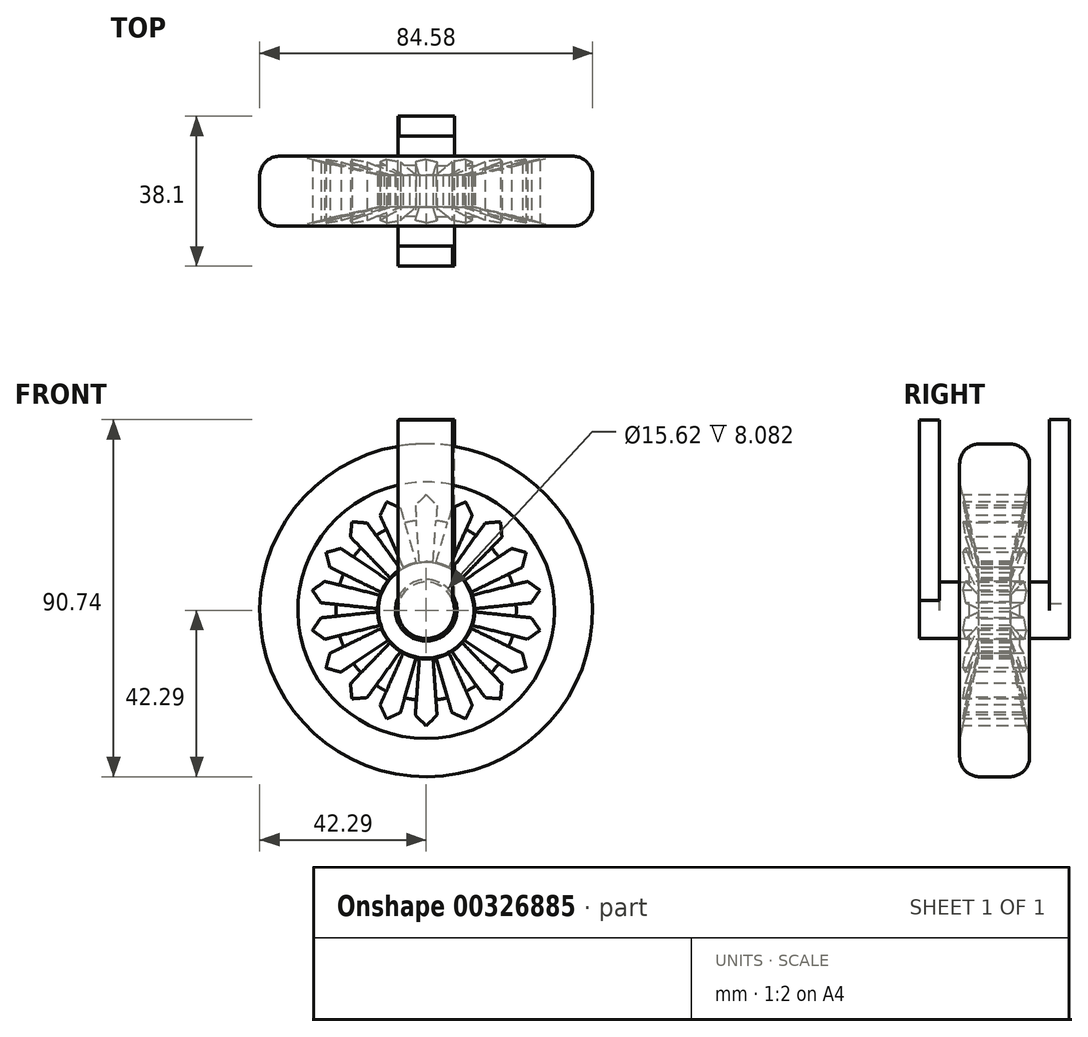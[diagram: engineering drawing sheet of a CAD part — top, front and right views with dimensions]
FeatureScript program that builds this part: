
annotation { "Feature Type Name" : "Feature", "Feature Type Description" : "" }
export const myFeature = defineFeature(function(context is Context, id is Id, definition is map)
    precondition{}
    {
        {
            var Q0;
            Q0=qCreatedBy(makeId("Right.planeOp"),FACE);
            var sketch = newSketch(context, id + "F0", { "sketchPlane" : qUnion([Q0])});
            skPoint(sketch, "E0.middle", {"position": v(0, 21.28) * mm});
            skLineSegment(sketch, "E1.bottom", {"start": v(8.9, 42.3) * mm, "end": v(-8.9, 42.3) * mm});
            skLineSegment(sketch, "E1.left", {"start": v(8.9, 42.3) * mm, "end": v(8.9, 32.6) * mm});
            skLineSegment(sketch, "E1.right", {"start": v(-8.9, 42.3) * mm, "end": v(-8.9, 32.6) * mm});
            skPoint(sketch, "E1.middle", {"position": v(0, 32.6) * mm});
            skLineSegment(sketch, "E2.bottom", {"start": v(4.04, 7.81) * mm, "end": v(-4.04, 7.81) * mm});
            skLineSegment(sketch, "E2.left", {"start": v(4.04, 7.81) * mm, "end": v(4.04, 9.97) * mm});
            skLineSegment(sketch, "E2.right", {"start": v(-4.04, 7.81) * mm, "end": v(-4.04, 9.97) * mm});
            skPoint(sketch, "E2.middle", {"position": v(0, 9.97) * mm});
            skPoint(sketch, "E3.orphan", {"position": v(6.47, 32.6) * mm});
            skPoint(sketch, "E4.orphan", {"position": v(-6.47, 32.6) * mm});
            skPoint(sketch, "E5.orphan", {"position": v(-4.04, 12.12) * mm});
            skPoint(sketch, "E6.orphan", {"position": v(4.04, 12.12) * mm});
            skPoint(sketch, "E7.orphan", {"position": v(-8.9, 22.9) * mm});
            skPoint(sketch, "E1.top.start.orphan", {"position": v(8.9, 22.9) * mm});
            skLineSegment(sketch, "E8", {"start": v(-4.04, 9.97) * mm, "end": v(-4.04, 12.12) * mm});
            skLineSegment(sketch, "E9", {"start": v(4.04, 9.97) * mm, "end": v(4.04, 12.12) * mm});
            skLineSegment(sketch, "E10", {"start": v(4.04, 12.12) * mm, "end": v(6.47, 22.9) * mm});
            skLineSegment(sketch, "E11", {"start": v(8.9, 32.6) * mm, "end": v(6.47, 22.9) * mm});
            skLineSegment(sketch, "E12", {"start": v(-8.9, 32.6) * mm, "end": v(-6.47, 22.9) * mm});
            skLineSegment(sketch, "E13", {"start": v(-6.47, 22.9) * mm, "end": v(-4.04, 12.12) * mm});
            skPoint(sketch, "E0.right.end.orphan", {"position": v(-6.47, 9.97) * mm});
            skPoint(sketch, "E0.left.end.orphan", {"position": v(6.47, 9.97) * mm});
            skLineSegment(sketch, "E14", {"start": v(-3.92, 0) * mm, "end": v(4.17, 0) * mm, "construction": true});
            skSolve(sketch);
        }
        {
            var Q0;
            Q0=makeQuery(id+"F0.imprint","IMPRINT",FACE,{"disambiguationData":[TD([[makeQuery(id+"F0.imprint","IMPRINT",EDGE,{"derivedFrom":sQuery(id+"F0.wireOp",EDGE,"E1.bottom")}),1.0]])]});
            var Q1;
            Q1=sQuery(id+"F0.wireOp",EDGE,"E14");
            revolve(context, id + "F1", {"entities" : qUnion([Q0]), "axis" : qUnion([Q1]), "revolveType" : RevolveType.FULL});
        }
        {
            var Q0;
            Q0=qCreatedBy(makeId("Front.planeOp"),FACE);
            var sketch = newSketch(context, id + "F2", { "sketchPlane" : qUnion([Q0])});
            skLineSegment(sketch, "E15", {"start": v(-1.74, 12.25) * mm, "end": v(-2.76, 26.64) * mm});
            skLineSegment(sketch, "E16", {"start": v(-2.76, 26.64) * mm, "end": v(0, 29.36) * mm});
            skLineSegment(sketch, "E17", {"start": v(-1.74, 12.25) * mm, "end": v(0, 12.38) * mm});
            skLineSegment(sketch, "E18.MirrorCS", {"start": v(2.76, 26.64) * mm, "end": v(0, 29.36) * mm});
            skLineSegment(sketch, "E19.MirrorCS", {"start": v(1.74, 12.25) * mm, "end": v(2.76, 26.64) * mm});
            skLineSegment(sketch, "E20.MirrorCS", {"start": v(1.74, 12.25) * mm, "end": v(0, 12.38) * mm});
            skSolve(sketch);
        }
        {
            var Q0;
            Q0 = qSketchRegion(id + "F2", true);
            extrude(context, id + "F3", {"entities" : qUnion([Q0]), "operationType" : NewBodyOperationType.REMOVE, "endBound" : BoundingType.SYMMETRIC, "oppositeDirection" : true, "depth" : 25.4 * mm});
        }
        {
            var Q0;
            Q0=makeQuery(id+"F3.boolean.opBoolean","COPY",FACE,{"derivedFrom":makeQuery(id+"F3.opExtrude","SWEPT_FACE",FACE,{"disambiguationData":[OSD([sQuery(id+"F2.wireOp",EDGE,"E16")])]})});
            var Q1;
            Q1=makeQuery(id+"F3.boolean.opBoolean","COPY",FACE,{"derivedFrom":makeQuery(id+"F3.opExtrude","SWEPT_FACE",FACE,{"disambiguationData":[OSD([sQuery(id+"F2.wireOp",EDGE,"E18.MirrorCS")])]})});
            var Q2;
            Q2=makeQuery(id+"F3.boolean.opBoolean","COPY",FACE,{"derivedFrom":makeQuery(id+"F3.opExtrude","SWEPT_FACE",FACE,{"disambiguationData":[OSD([sQuery(id+"F2.wireOp",EDGE,"E15")])]})});
            var Q3;
            Q3=makeQuery(id+"F3.boolean.opBoolean","COPY",FACE,{"derivedFrom":makeQuery(id+"F3.opExtrude","SWEPT_FACE",FACE,{"disambiguationData":[OSD([sQuery(id+"F2.wireOp",EDGE,"E17")])]})});
            var Q4;
            Q4=makeQuery(id+"F3.boolean.opBoolean","COPY",FACE,{"derivedFrom":makeQuery(id+"F3.opExtrude","SWEPT_FACE",FACE,{"disambiguationData":[OSD([sQuery(id+"F2.wireOp",EDGE,"E20.MirrorCS")])]})});
            var Q5;
            Q5=makeQuery(id+"F3.boolean.opBoolean","COPY",FACE,{"derivedFrom":makeQuery(id+"F3.opExtrude","SWEPT_FACE",FACE,{"disambiguationData":[OSD([sQuery(id+"F2.wireOp",EDGE,"E19.MirrorCS")])]})});
            var Q6;
            Q6=makeQuery(id+"F1.opRevolve","SWEPT_FACE",FACE,{"disambiguationData":[OSD([sQuery(id+"F0.wireOp",EDGE,"E13")])]});
            circularPattern(context, id + "F4", {"patternType" : PatternType.FACE, "faces" : qUnion([Q0, Q1, Q2, Q3, Q4, Q5]), "axis" : qUnion([Q6]), "angle" : 360 * degree, "instanceCount" : 18, "equalSpace" : true});
        }
        {
            var Q0;
            Q0=makeQuery(id+"F1.opRevolve","SWEPT_FACE",FACE,{"disambiguationData":[OSD([sQuery(id+"F0.wireOp",EDGE,"E1.bottom")])]});
            var Q1;
            Q1=makeQuery(id+"F1.opRevolve","SWEPT_FACE",FACE,{"disambiguationData":[OSD([sQuery(id+"F0.wireOp",EDGE,"E1.left")])]});
            var Q2;
            Q2=makeQuery(id+"F1.opRevolve","SWEPT_EDGE",EDGE,{"disambiguationData":[OSD([sQuery(id+"F0.wireOp",EDGE,"E1.left"),sQuery(id+"F0.wireOp",EDGE,"E11")])]});
            fillet(context, id + "F5", {"entities" : qUnion([Q0, Q1, Q2]), "radius" : 5.08 * mm, "tangentPropagation" : true, "allowEdgeOverflow" : false});
        }
        {
            var Q0;
            Q0=qCreatedBy(makeId("Front.planeOp"),FACE);
            var sketch = newSketch(context, id + "F6", { "sketchPlane" : qUnion([Q0])});
            skCircle(sketch, "E21", {"center": v(0, 0) * mm, "radius": 7.17 * mm});
            skLineSegment(sketch, "E22.bottom", {"start": v(-7.17, 0) * mm, "end": v(-7.21, 0) * mm});
            skPoint(sketch, "E23.orphan", {"position": v(7.17, 0) * mm});
            skSolve(sketch);
        }
        {
            var Q0;
            Q0=makeQuery(id+"F6.imprint","IMPRINT",FACE,{"disambiguationData":[TD([[makeQuery(id+"F6.imprint","IMPRINT",EDGE,{"derivedFrom":sQuery(id+"F6.wireOp",EDGE,"E21")}),1.0]])]});
            extrude(context, id + "F7", {"entities" : qUnion([Q0]), "endBound" : BoundingType.SYMMETRIC, "depth" : 38.1 * mm});
        }
        {
            var Q0;
            Q0=makeQuery(id+"F7.opExtrude","CAP_FACE",FACE,{"disambiguationData":[OSD([sQuery(id+"F6.wireOp",EDGE,"E21")])],"isStart":false});
            var sketch = newSketch(context, id + "F8", { "sketchPlane" : qUnion([Q0])});
            skLineSegment(sketch, "E24.bottom", {"start": v(-7.17, 0) * mm, "end": v(6.73, 0) * mm});
            skLineSegment(sketch, "E24.top", {"start": v(-7.17, 48.33) * mm, "end": v(6.73, 48.33) * mm});
            skLineSegment(sketch, "E24.left", {"start": v(-7.17, 0) * mm, "end": v(-7.17, 48.33) * mm});
            skLineSegment(sketch, "E24.right", {"start": v(6.73, 0) * mm, "end": v(6.73, 48.33) * mm});
            skSolve(sketch);
        }
        {
            var Q0;
            {var subQ0=sQuery(id+"F8.wireOp",EDGE,"E24.top");Q0=makeQuery(id+"F8.imprint","IMPRINT",FACE,{"disambiguationData":[TD([[makeQuery(id+"F8.imprint","IMPRINT",EDGE,{"derivedFrom":subQ0}),-1.0]])]});}
            extrude(context, id + "F9", {"entities" : qUnion([Q0]), "operationType" : NewBodyOperationType.ADD, "oppositeDirection" : true, "depth" : 5.08 * mm});
        }
        {
            var Q0;
            Q0=makeQuery(id+"F7.opExtrude","CAP_FACE",FACE,{"disambiguationData":[OSD([sQuery(id+"F6.wireOp",EDGE,"E21")])],"isStart":true});
            var sketch = newSketch(context, id + "F10", { "sketchPlane" : qUnion([Q0])});
            skLineSegment(sketch, "E25.bottom", {"start": v(-7.17, 0) * mm, "end": v(6.94, 0) * mm});
            skLineSegment(sketch, "E25.top", {"start": v(-7.17, 48.45) * mm, "end": v(6.94, 48.45) * mm});
            skLineSegment(sketch, "E25.left", {"start": v(-7.17, 0) * mm, "end": v(-7.17, 48.45) * mm});
            skLineSegment(sketch, "E25.right", {"start": v(6.94, 0) * mm, "end": v(6.94, 48.45) * mm});
            skSolve(sketch);
        }
        {
            var Q0;
            Q0 = qSketchRegion(id + "F10", true);
            extrude(context, id + "F11", {"entities" : qUnion([Q0]), "operationType" : NewBodyOperationType.ADD, "oppositeDirection" : true, "depth" : 5.08 * mm});
        }
    });
